# Revit family: P190780JX-152c_JMC2427IL_StainlessSteel_JA_Cooking_Microwaves
name_source: partatom
category: Specialty Equipment
units: mm (PartAtom-declared; Revit-internal decimal feet)

## family parameters
Always vertical = Yes
Cut with Voids When Loaded = No
Enable Cutting in Views = No
Maintain Annotation Orientation = No
Part Type = Normal
Room Calculation Point = No
Round Connector Dimension = Use Diameter
Shared = No
Work Plane-Based = No

## types (1)
- JMC2427IL
    Amps = 0 A
    Body Material = ARCAT - Metal - Steel - Stainless
    Clearance Material = ARCAT - Clearance
    Default Elevation = 0"
    Depth = 25 1/2"
    Description = RISE™  27" BUILT-IN MICROWAVE OVEN WITH SPEED-COOK
Four à micro-ondes avec cuisson rapide RISE™, 27 po
    Display Panel Material = ARCAT - Glass - Black
    Door Material = ARCAT - Metal - Steel - Stainless
    Family Name = BUILT-IN MICROWAVES - 27"
    Feature 1 = 4.3-Inch Full Color LCD Display
Affichage en couleur ACL de 4,3 po
    Feature 2 = Seamless Touches
Détails discrets
    Feature 3 = Stainless Steel Microwave Interior
Intérieur de four à micro-ondes en acier inoxydable
    Glass Material = ARCAT - Glass - Tempered - Black
    Handle Material = ARCAT - Metal - Steel - Gray
    Height = 19 7/8"
    Installation-Fabrication = http://access.whirlpool.com Instruction&sku=JMC2427IL&language=EN
http://access.whirlpool.com Instruction&sku=JMC2427IL&language=EN
    Manufacturer = Jenn Air
    Model = JMC2427IL
    Voltage = 0 V
    Width = 26 3/4"

## geometry (parser evidence)
native form markers: Sweep x5
no freeform markers — native parametric forms only
